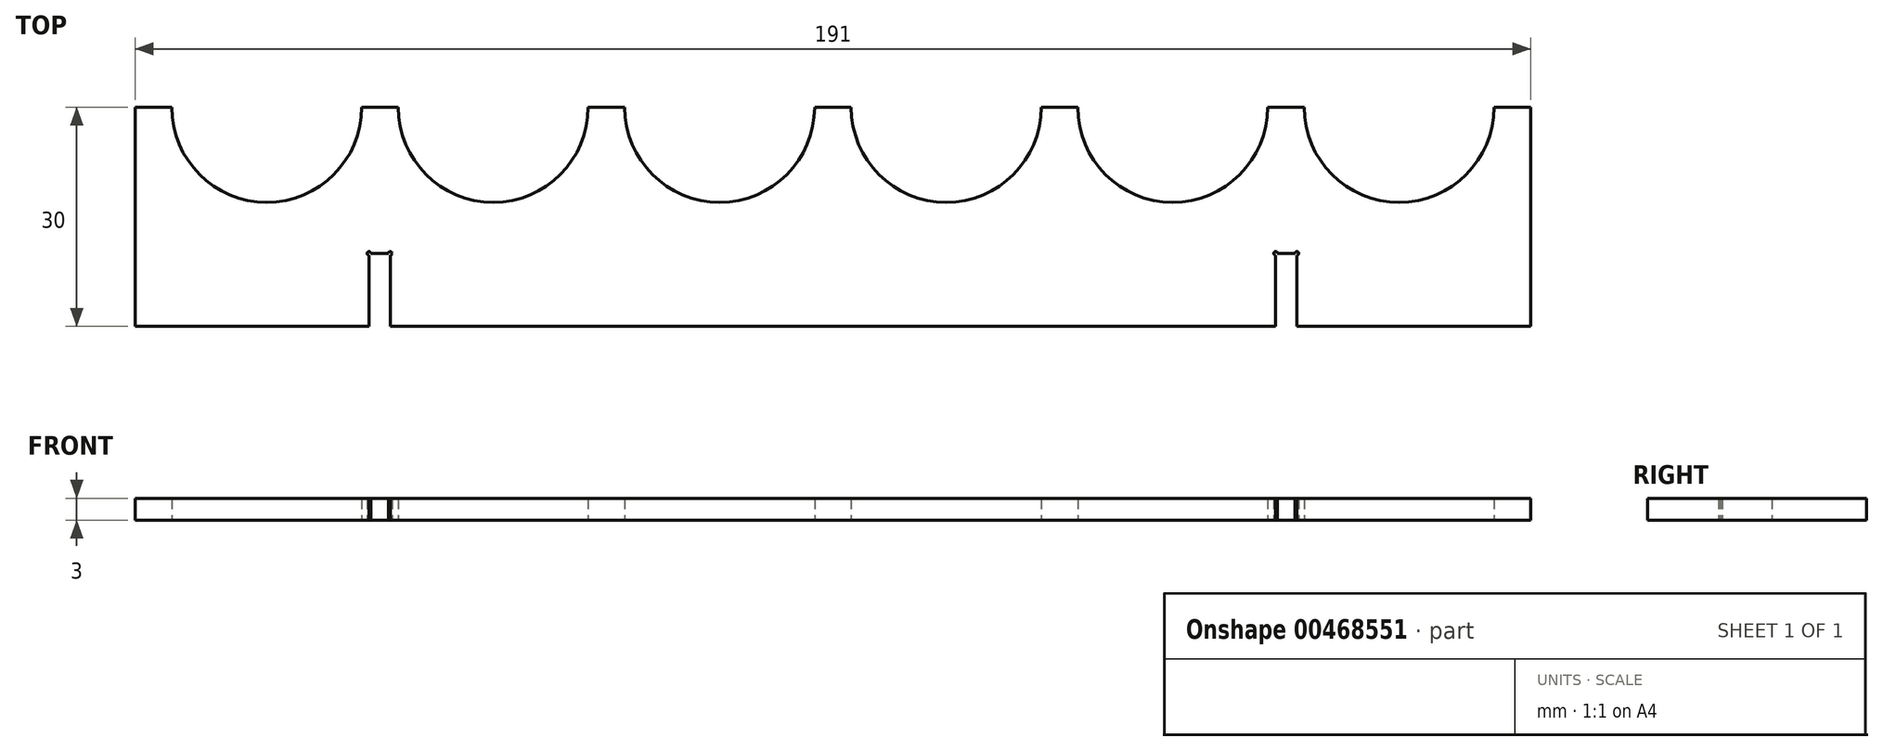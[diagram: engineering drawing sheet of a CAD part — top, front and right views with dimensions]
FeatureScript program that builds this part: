
annotation { "Feature Type Name" : "Feature", "Feature Type Description" : "" }
export const myFeature = defineFeature(function(context is Context, id is Id, definition is map)
    precondition{}
    {
        {
            var Q0;
            Q0=qCreatedBy(makeId("Top.planeOp"),FACE);
            var sketch = newSketch(context, id + "F0", { "sketchPlane" : qUnion([Q0])});
            skLineSegment(sketch, "E0.bottom", {"start": v(-95.5, 0) * mm, "end": v(95.5, 0) * mm});
            skLineSegment(sketch, "E0.top", {"start": v(-95.5, -30) * mm, "end": v(95.5, -30) * mm});
            skLineSegment(sketch, "E0.left", {"start": v(-95.5, 0) * mm, "end": v(-95.5, -30) * mm});
            skLineSegment(sketch, "E0.right", {"start": v(95.5, 0) * mm, "end": v(95.5, -30) * mm});
            skPoint(sketch, "E1", {"position": v(-95.5, 0) * mm});
            skPoint(sketch, "E2", {"position": v(-77.5, 0) * mm});
            skPoint(sketch, "E3", {"position": v(-46.5, 0) * mm});
            skPoint(sketch, "E4", {"position": v(-15.5, 0) * mm});
            skPoint(sketch, "E5", {"position": v(15.5, 0) * mm});
            skPoint(sketch, "E6", {"position": v(46.5, 0) * mm});
            skPoint(sketch, "E7", {"position": v(77.5, 0) * mm});
            skPoint(sketch, "E8", {"position": v(106.5, 0) * mm});
            skCircle(sketch, "E9", {"center": v(-77.5, 0) * mm, "radius": 13 * mm});
            skCircle(sketch, "E10", {"center": v(-46.5, 0) * mm, "radius": 13 * mm});
            skCircle(sketch, "E11", {"center": v(-15.5, 0) * mm, "radius": 13 * mm});
            skCircle(sketch, "E12", {"center": v(15.5, 0) * mm, "radius": 13 * mm});
            skCircle(sketch, "E13", {"center": v(46.5, 0) * mm, "radius": 13 * mm});
            skCircle(sketch, "E14", {"center": v(77.5, 0) * mm, "radius": 13 * mm});
            skPoint(sketch, "E15", {"position": v(-63.5, -30) * mm});
            skPoint(sketch, "E16", {"position": v(63.5, -30) * mm});
            skLineSegment(sketch, "E17", {"start": v(-63.5, -30) * mm, "end": v(-63.5, -20) * mm});
            skLineSegment(sketch, "E18", {"start": v(-63.5, -20) * mm, "end": v(-60.6, -20) * mm});
            skLineSegment(sketch, "E19", {"start": v(-60.6, -20) * mm, "end": v(-60.6, -30) * mm});
            skLineSegment(sketch, "E20", {"start": v(-60.6, -30) * mm, "end": v(63.5, -30) * mm});
            skLineSegment(sketch, "E21", {"start": v(63.5, -20) * mm, "end": v(60.6, -20) * mm});
            skLineSegment(sketch, "E22", {"start": v(60.6, -20) * mm, "end": v(60.6, -30) * mm});
            skLineSegment(sketch, "E23", {"start": v(63.5, -20) * mm, "end": v(63.5, -30) * mm});
            skCircle(sketch, "E24", {"center": v(-60.6, -20) * mm, "radius": 0.25 * mm});
            skCircle(sketch, "E25", {"center": v(-63.5, -20) * mm, "radius": 0.25 * mm});
            skCircle(sketch, "E26", {"center": v(63.5, -20) * mm, "radius": 0.25 * mm});
            skCircle(sketch, "E27", {"center": v(60.6, -20) * mm, "radius": 0.25 * mm});
            skSolve(sketch);
        }
        {
            var Q0;
            {var subQ24=sQuery(id+"F0.wireOp",EDGE,"E0.left");Q0=makeQuery(id+"F0.imprint","IMPRINT",FACE,{"disambiguationData":[TD([[makeQuery(id+"F0.imprint","IMPRINT",EDGE,{"derivedFrom":subQ24}),1.0]])]});}
            extrude(context, id + "F1", {"entities" : qUnion([Q0]), "depth" : 3 * mm, "offsetDistance" : 25 * mm});
        }
    });
